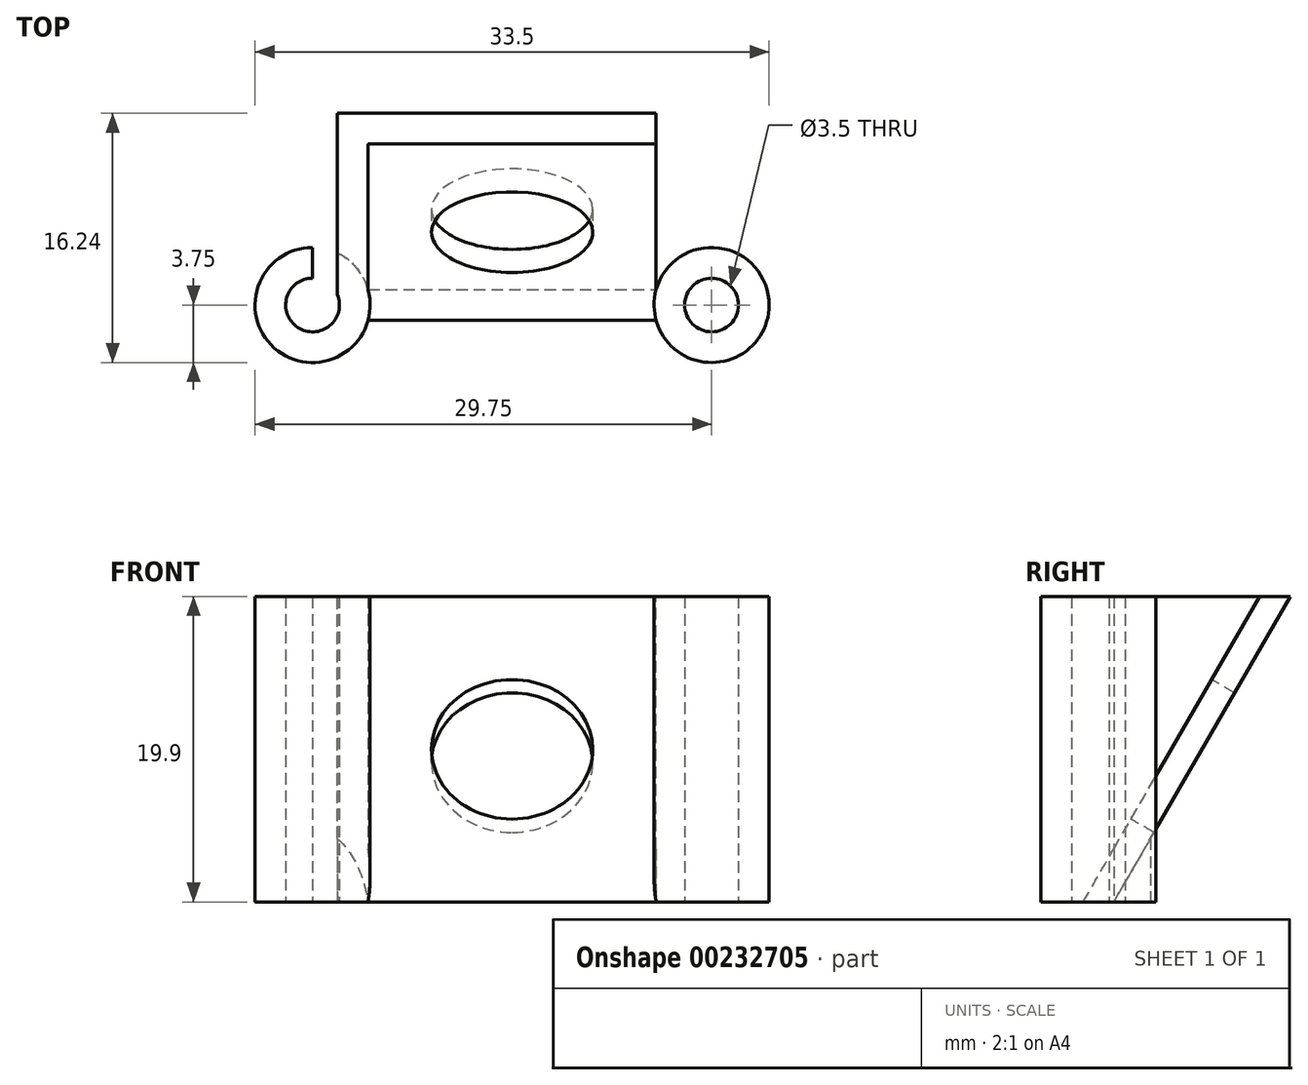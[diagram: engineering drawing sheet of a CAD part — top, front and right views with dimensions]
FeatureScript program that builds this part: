
annotation { "Feature Type Name" : "Feature", "Feature Type Description" : "" }
export const myFeature = defineFeature(function(context is Context, id is Id, definition is map)
    precondition{}
    {
        {
            var Q0;
            Q0=qCreatedBy(makeId("Top.planeOp"),FACE);
            var sketch = newSketch(context, id + "F0", { "sketchPlane" : qUnion([Q0])});
            skLineSegment(sketch, "E0", {"start": v(-13, 0) * mm, "end": v(13, 0) * mm, "construction": true});
            skCircle(sketch, "E1", {"center": v(-13, 0) * mm, "radius": 1.75 * mm});
            skCircle(sketch, "E2", {"center": v(13, 0) * mm, "radius": 1.75 * mm});
            skCircle(sketch, "E3.0", {"center": v(13, 0) * mm, "radius": 3.75 * mm});
            skCircle(sketch, "E4.0", {"center": v(-13, 0) * mm, "radius": 3.75 * mm});
            skSolve(sketch);
        }
        {
            var Q0;
            Q0 = qSketchRegion(id + "F0", true);
            extrude(context, id + "F1", {"entities" : qUnion([Q0]), "depth" : 19.9 * mm});
        }
        {
            var Q0;
            Q0=qCreatedBy(makeId("Top.planeOp"),FACE);
            var sketch = newSketch(context, id + "F2", { "sketchPlane" : qUnion([Q0])});
            skLineSegment(sketch, "E5.bottom", {"start": v(-9.39, 1) * mm, "end": v(9.39, 1) * mm});
            skLineSegment(sketch, "E5.top", {"start": v(-9.39, -1) * mm, "end": v(9.39, -1) * mm});
            skLineSegment(sketch, "E5.left", {"start": v(-9.39, 1) * mm, "end": v(-9.39, -1) * mm});
            skLineSegment(sketch, "E5.right", {"start": v(9.39, 1) * mm, "end": v(9.39, -1) * mm});
            skPoint(sketch, "E5.middle", {"position": v(0, 0) * mm});
            skSolve(sketch);
        }
        {
            var Q0;
            Q0=qCreatedBy(makeId("Right.planeOp"),FACE);
            var sketch = newSketch(context, id + "F3", { "sketchPlane" : qUnion([Q0])});
            skLineSegment(sketch, "E6", {"start": v(0, 0) * mm, "end": v(11.49, 19.9) * mm, "construction": true});
            skLineSegment(sketch, "E7", {"start": v(11.49, 19.9) * mm, "end": v(7.42, 19.9) * mm, "construction": true});
            skSolve(sketch);
        }
        {
            var Q0;
            Q0=makeQuery(id+"F1.opExtrude","CAP_FACE",FACE,{"disambiguationData":[OSD([sQuery(id+"F0.wireOp",EDGE,"E1"),sQuery(id+"F0.wireOp",EDGE,"E4.0")])],"isStart":false});
            cPlane(context, id + "F4", {"entities" : qUnion([Q0]), "cplaneType" : CPlaneType.OFFSET, "offset" : 0 * mm, "width" : 150 * mm, "height" : 150 * mm});
        }
        {
            var Q0;
            Q0=qCreatedBy(id+"F4.planeOp",FACE);
            var sketch = newSketch(context, id + "F5", { "sketchPlane" : qUnion([Q0])});
            skLineSegment(sketch, "E8.bottom", {"start": v(9.39, 10.49) * mm, "end": v(-9.39, 10.49) * mm});
            skLineSegment(sketch, "E8.top", {"start": v(9.39, 12.49) * mm, "end": v(-9.39, 12.49) * mm});
            skLineSegment(sketch, "E8.left", {"start": v(9.39, 10.49) * mm, "end": v(9.39, 12.49) * mm});
            skLineSegment(sketch, "E8.right", {"start": v(-9.39, 10.49) * mm, "end": v(-9.39, 12.49) * mm});
            skPoint(sketch, "E8.middle", {"position": v(0, 11.49) * mm});
            skSolve(sketch);
        }
        {
            var Q0;
            Q0 = qSketchRegion(id + "F2", true);
            var Q1;
            Q1 = qSketchRegion(id + "F5", true);
            loft(context, id + "F6", {"operationType" : NewBodyOperationType.ADD, "sheetProfilesArray" : [{ "sheetProfileEntities" : qUnion([Q0]) }, { "sheetProfileEntities" : qUnion([Q1]) }]});
        }
        {
            var Q0;
            Q0=makeQuery(id+"F6.opLoft","SWEPT_FACE",FACE,{"disambiguationData":[OSD([sQuery(id+"F2.wireOp",EDGE,"E5.top"),sQuery(id+"F2.wireOp",EDGE,"E5.left"),sQuery(id+"F2.wireOp",EDGE,"E5.right"),sQuery(id+"F5.wireOp",EDGE,"E8.bottom"),sQuery(id+"F5.wireOp",EDGE,"E8.left"),sQuery(id+"F5.wireOp",EDGE,"E8.right")])]});
            cPlane(context, id + "F7", {"entities" : qUnion([Q0]), "cplaneType" : CPlaneType.OFFSET, "offset" : 0 * mm, "width" : 150 * mm, "height" : 150 * mm});
        }
        {
            var Q0;
            Q0=qCreatedBy(id+"F7.planeOp",FACE);
            var sketch = newSketch(context, id + "F8", { "sketchPlane" : qUnion([Q0])});
            skLineSegment(sketch, "E9", {"start": v(-9.39, 22.48) * mm, "end": v(9.39, -0.5) * mm, "construction": true});
            skCircle(sketch, "E10", {"center": v(0, 10.99) * mm, "radius": 5.25 * mm});
            skSolve(sketch);
        }
        {
            var Q0;
            Q0 = qSketchRegion(id + "F8", true);
            extrude(context, id + "F9", {"entities" : qUnion([Q0]), "operationType" : NewBodyOperationType.REMOVE, "endBound" : BoundingType.THROUGH_ALL, "oppositeDirection" : true, "depth" : 25 * mm});
        }
        {
            var Q0;
            Q0=makeQuery(id+"F6.opLoft","SWEPT_FACE",FACE,{"disambiguationData":[OSD([sQuery(id+"F2.wireOp",EDGE,"E5.bottom"),sQuery(id+"F2.wireOp",EDGE,"E5.top"),sQuery(id+"F2.wireOp",EDGE,"E5.left"),sQuery(id+"F5.wireOp",EDGE,"E8.bottom"),sQuery(id+"F5.wireOp",EDGE,"E8.top"),sQuery(id+"F5.wireOp",EDGE,"E8.right")])]});
            var sketch = newSketch(context, id + "F10", { "sketchPlane" : qUnion([Q0])});
            skLineSegment(sketch, "E11", {"start": v(-12.49, 19.9) * mm, "end": v(-1, 0) * mm});
            skLineSegment(sketch, "E12", {"start": v(-1, 0) * mm, "end": v(-1, 3.46) * mm});
            skLineSegment(sketch, "E13", {"start": v(-1, 3.46) * mm, "end": v(-1, 19.9) * mm});
            skLineSegment(sketch, "E14", {"start": v(-1, 19.9) * mm, "end": v(-12.49, 19.9) * mm});
            skSolve(sketch);
        }
        {
            var Q0;
            Q0 = qSketchRegion(id + "F10", true);
            extrude(context, id + "F11", {"entities" : qUnion([Q0]), "operationType" : NewBodyOperationType.ADD, "depth" : 2 * mm});
        }
        {
            var Q0;
            Q0=qCreatedBy(makeId("Top.planeOp"),FACE);
            var sketch = newSketch(context, id + "F12", { "sketchPlane" : qUnion([Q0])});
            skCircle(sketch, "E15.0", {"center": v(-13, 0) * mm, "radius": 1.75 * mm, "construction": true});
            skLineSegment(sketch, "E16.bottom", {"start": v(-13, 0) * mm, "end": v(-11.39, 0) * mm});
            skLineSegment(sketch, "E16.top", {"start": v(-13, 7) * mm, "end": v(-11.39, 7) * mm});
            skLineSegment(sketch, "E16.left", {"start": v(-13, 0) * mm, "end": v(-13, 7) * mm});
            skLineSegment(sketch, "E16.right", {"start": v(-11.39, 0) * mm, "end": v(-11.39, 7) * mm});
            skSolve(sketch);
        }
        {
            var Q0;
            Q0 = qSketchRegion(id + "F12", true);
            extrude(context, id + "F13", {"entities" : qUnion([Q0]), "operationType" : NewBodyOperationType.REMOVE, "endBound" : BoundingType.THROUGH_ALL, "depth" : 25 * mm});
        }
    });
